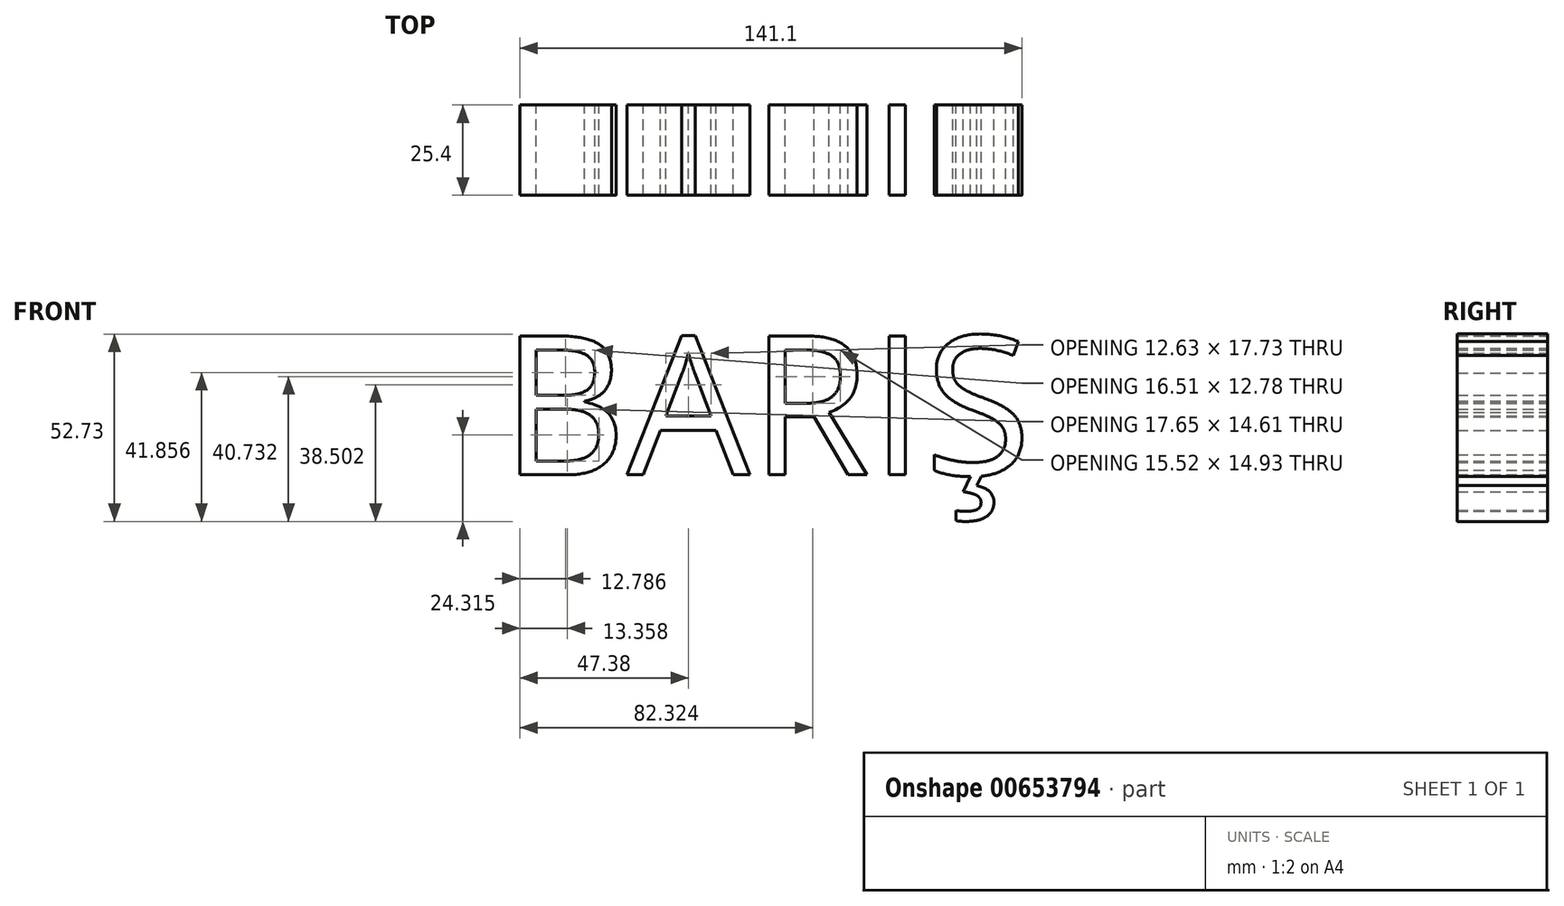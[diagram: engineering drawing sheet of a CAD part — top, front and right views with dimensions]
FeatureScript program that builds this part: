
annotation { "Feature Type Name" : "Feature", "Feature Type Description" : "" }
export const myFeature = defineFeature(function(context is Context, id is Id, definition is map)
    precondition{}
    {
        {
            var Q0;
            Q0=qCreatedBy(makeId("Front.planeOp"),FACE);
            var sketch = newSketch(context, id + "F0", { "sketchPlane" : qUnion([Q0])});
            skText(sketch, "E0", { "text": "BARIŞ", "fontName": "OpenSans-Regular.ttf"});
            const initialGuessF0  = {"E0": [-0.0748, -0.02086, 1, 0, 0.03937]};
            skSetInitialGuess(sketch, initialGuessF0);
            skSolve(sketch);
        }
        {
            var Q0;
            Q0 = qSketchRegion(id + "F0", true);
            extrude(context, id + "F1", {"entities" : qUnion([Q0]), "depth" : 25.4 * mm, "offsetDistance" : 25.4 * mm});
        }
    });
